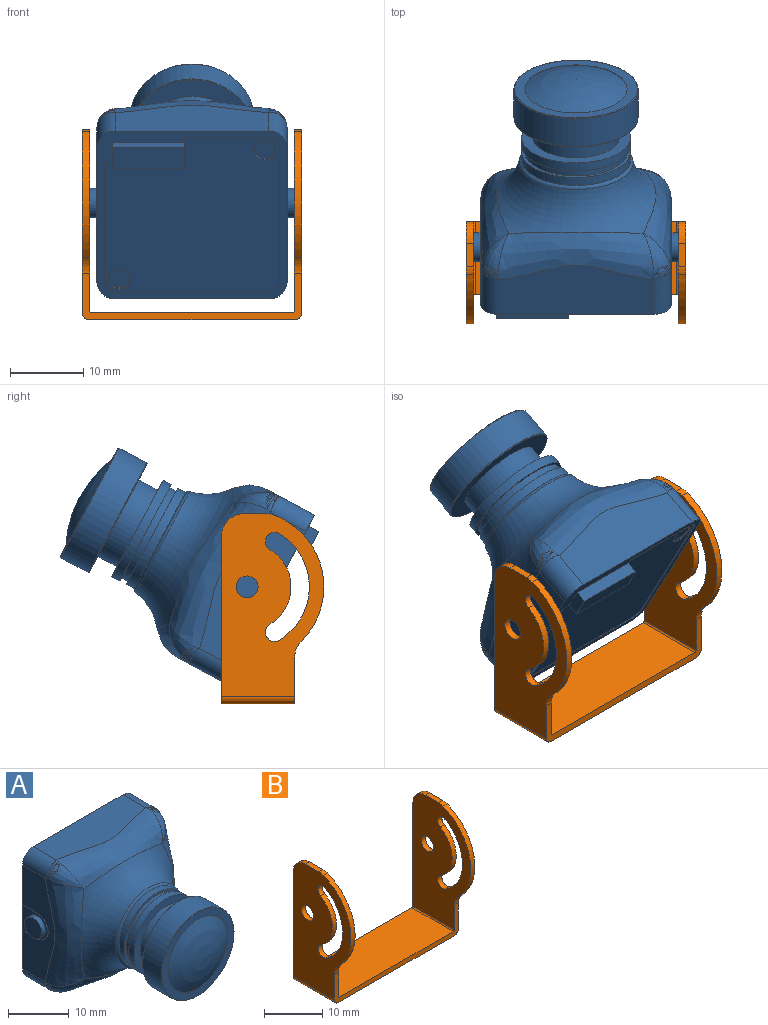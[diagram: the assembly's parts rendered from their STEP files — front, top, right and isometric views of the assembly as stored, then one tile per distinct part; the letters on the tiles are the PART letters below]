
ASSEMBLY  parts=2 mates=1
PART A: 86 faces, bbox 33.8x31.1x33.8 mm
  f0: torus R=12.35mm, axis (0,1,0), area 0mm2, adj f7,f31,f34
  f1: torus R=12.35mm, axis (0,1,0), area 0mm2, adj f8,f23,f26
  f2: torus R=12.35mm, axis (0,1,0), area 0mm2, adj f6,f28,f30
  f3: torus R=15.6mm, axis (0,1,0), area 402.5mm2, adj f5,f15,f16,f17,f18
  f4: torus R=12.35mm, axis (0,1,0), area 0mm2, adj f9,f19,f22
  f5: torus R=7.32mm, axis (0,1,0), area 33.3mm2, adj f3,f66
  f6: cylinder r=2.5mm len=5.66mm, axis (0,1,0), area 22mm2, adj f2,f10,f13,f14,f16,f18,f28,f30
  f7: cylinder r=2.5mm len=5.66mm, axis (0,1,0), area 22mm2, adj f0,f10,f11,f14,f17,f18,f31,f34
  f8: cylinder r=2.5mm len=5.66mm, axis (0,1,0), area 22mm2, adj f1,f11,f12,f14,f15,f17,f23,f26
  f9: cylinder r=2.5mm len=5.66mm, axis (0,1,0), area 22mm2, adj f4,f12,f13,f14,f15,f16,f19,f22
  f10: plane 21.01x7.56mm, normal (0,0,-1), area 137.3mm2, adj f6,f7,f14,f18
  f11: plane 21x7.56mm, normal (-1,0,0), area 109.5mm2, adj f7,f8,f14,f17,f58,f59,f60
  f12: plane 21x7.56mm, normal (0,0,1), area 137.3mm2, adj f8,f9,f14,f15
  f13: plane 21.01x7.56mm, normal (1,0,0), area 109.5mm2, adj f6,f9,f14,f16,f55,f56,f57
  f14: plane 26.25x26mm, normal (0,1,0), area 108.7mm2, adj f6,f7,f8,f9,f10,f11,f12,f13
  f15: bspline ~24.08x6.44mm, area 116mm2, adj f3,f8,f9,f12,f20,f22,f23,f24
  f16: bspline ~24.08x6.44mm, area 116mm2, adj f3,f6,f9,f13,f19,f20,f27,f28
  f17: bspline ~24.08x6.44mm, area 116mm2, adj f3,f7,f8,f11,f24,f26,f31,f32
  f18: bspline ~24.08x6.44mm, area 116mm2, adj f3,f6,f7,f10,f27,f30,f32,f34
  f19: bspline ~1.79x1.79mm, area 1.2mm2, adj f4,f9,f16,f21
  f20: bspline ~5.02x3.83mm, area 8.7mm2, adj f15,f16,f21
  f21: sphere r=2.4mm, area 2mm2, adj f19,f20,f22
  f22: bspline ~1.79x1.79mm, area 1.2mm2, adj f4,f9,f15,f21
  f23: bspline ~1.79x1.79mm, area 1.2mm2, adj f1,f8,f15,f25
  f24: bspline ~5.02x3.83mm, area 8.7mm2, adj f15,f17,f25
  f25: sphere r=2.4mm, area 2mm2, adj f23,f24,f26
  f26: bspline ~1.79x1.79mm, area 1.2mm2, adj f1,f8,f17,f25
  f27: bspline ~5.02x3.83mm, area 8.7mm2, adj f16,f18,f29
  f28: bspline ~1.79x1.79mm, area 1.2mm2, adj f2,f6,f16,f29
  f29: sphere r=2.4mm, area 2mm2, adj f27,f28,f30
  f30: bspline ~1.79x1.79mm, area 1.2mm2, adj f2,f6,f18,f29
  f31: bspline ~1.79x1.79mm, area 1.2mm2, adj f0,f7,f17,f33
  f32: bspline ~5.02x3.83mm, area 8.7mm2, adj f17,f18,f33
  f33: sphere r=2.4mm, area 2mm2, adj f31,f32,f34
  f34: bspline ~1.79x1.79mm, area 1.2mm2, adj f0,f7,f18,f33
  f35: plane 11.5x0.1mm, normal (0,0,1), area 1.1mm2, adj f14,f36,f43,f44
  f36: plane 4x1.7mm, normal (1,0,0), area 5.7mm2, adj f14,f35,f37,f44,f52,f53
  f37: plane 11x1.7mm, normal (0,0,1), area 16.9mm2, adj f14,f36,f38,f44,f51,f53
  f38: plane 18.5x0.1mm, normal (1,0,0), area 1.8mm2, adj f14,f37,f39,f44
  f39: cylinder r=1.5mm len=1.5mm, axis (0,1,0), area 0.2mm2, adj f14,f38,f40,f44
  f40: plane 21x0.1mm, normal (0,0,-1), area 2.1mm2, adj f14,f39,f41,f44
  f41: cylinder r=1.5mm len=1.5mm, axis (0,1,0), area 0.2mm2, adj f14,f40,f42,f44
  f42: plane 21x0.1mm, normal (-1,0,0), area 2.1mm2, adj f14,f41,f43,f44
  f43: cylinder r=1.5mm len=1.5mm, axis (0,1,0), area 0.2mm2, adj f14,f35,f42,f44
  f44: plane 24x24mm, normal (0,1,0), area 516.4mm2, adj f35,f36,f37,f38,f39,f40,f41,f42
  f45: cylinder r=1.4mm len=2.8mm, axis (0,1,0), area 0.9mm2, adj f46,f49
  f46: plane 2.8x2.8mm, normal (0,1,0), area 6.2mm2, adj f45
  f47: cylinder r=1.4mm len=2.8mm, axis (0,1,0), area 0.9mm2, adj f48,f50
  f48: plane 2.8x2.8mm, normal (0,1,0), area 6.2mm2, adj f47
  f49: cone r=1.4mm half-angle=45deg, axis (0,1,0), area 1.3mm2, adj f44,f45
  f50: cone r=1.4mm half-angle=45deg, axis (0,1,0), area 1.3mm2, adj f44,f47
  f51: plane 3.3x1.6mm, normal (-1,0,0), area 5.3mm2, adj f14,f37,f52,f53
  f52: plane 9.9x1.6mm, normal (0,0,-1), area 15.8mm2, adj f14,f36,f51,f53
  f53: plane 9.9x3.3mm, normal (0,1,0), area 32.7mm2, adj f36,f37,f51,f52
  f54: plane 6x5.3mm, normal (1,0,0), area 15.3mm2, adj f14,f55,f56,f57,f64
  f55: cylinder r=2.5mm len=5mm, axis (-1,0,0), area 1mm2, adj f13,f54,f56,f57
  f56: plane 3.61x0.15mm, normal (0,-0.04,1), area 0.5mm2, adj f13,f14,f54,f55
  f57: plane 3.61x0.15mm, normal (0,-0.04,-1), area 0.5mm2, adj f13,f14,f54,f55
  f58: plane 3.61x0.15mm, normal (0,-0.04,-1), area 0.5mm2, adj f11,f14,f60,f61
  f59: plane 3.61x0.15mm, normal (0,-0.04,1), area 0.5mm2, adj f11,f14,f60,f61
  f60: cylinder r=2.5mm len=5mm, axis (-1,0,0), area 1mm2, adj f11,f58,f59,f61
  f61: plane 6x5.3mm, normal (-1,0,0), area 15.3mm2, adj f14,f58,f59,f60,f63
  f62: plane 4x4mm, normal (-1,0,0), area 12.6mm2, adj f63
  f63: cylinder r=2mm len=4mm, axis (-1,0,0), area 11mm2, adj f61,f62
  f64: cylinder r=2mm len=4mm, axis (-1,0,0), area 11mm2, adj f54,f65
  f65: plane 4x4mm, normal (1,0,0), area 12.6mm2, adj f64
  f66: plane 14.9x14.9mm, normal (0,1,0), area 6mm2, adj f5,f67
  f67: cylinder r=7.45mm len=14.9mm, axis (0,1,0), area 58.5mm2, adj f66,f69
  f68: plane 14.9x14.9mm, normal (0,1,0), area 20.4mm2, adj f70,f78
  f69: plane 14.9x14.9mm, normal (0,-1,0), area 20.4mm2, adj f67,f70
  f70: cylinder r=7mm len=14mm, axis (0,-1,0), area 44mm2, adj f68,f69
  f71: sphere r=16mm, area 162.1mm2, adj f72
  f72: cylinder r=7mm len=14mm, axis (0,-1,0), area 4.4mm2, adj f71,f73
  f73: plane 16.8x16.8mm, normal (0,-1,0), area 67.7mm2, adj f72,f80
  f74: cylinder r=8.5mm len=17mm, axis (0,1,0), area 229.7mm2, adj f79,f80
  f75: plane 16.8x16.8mm, normal (0,1,0), area 111.4mm2, adj f76,f79
  f76: cylinder r=5.92mm len=11.85mm, axis (0,1,0), area 111.7mm2, adj f75,f77
  f77: plane 14.9x14.9mm, normal (0,-1,0), area 64.1mm2, adj f76,f78
  f78: cylinder r=7.45mm len=14.9mm, axis (0,1,0), area 58.5mm2, adj f68,f77
  f79: torus R=8.4mm, axis (0,-1,0), area 8.4mm2, adj f74,f75
  f80: torus R=8.4mm, axis (0,-1,0), area 8.4mm2, adj f73,f74
  f81: plane 11.15x3.93mm, normal (0,-1,0), area 31.9mm2, adj f83,f84
  f82: plane 11.15x3.93mm, normal (0,-1,0), area 31.9mm2, adj f83,f84
  f83: cylinder r=2.5mm len=11.15mm, axis (-1,0,0), area 51.7mm2, adj f81,f82,f84
  f84: cylinder r=5.92mm len=12mm, axis (0,-1,0), area 446.7mm2, adj f81,f82,f83,f85
  f85: plane 11.85x11.85mm, normal (0,1,0), area 110.3mm2, adj f84
PART B: 32 faces, bbox 30x14x26 mm
  f0: plane 3.19x1mm, normal (0,0,1), area 3.2mm2, adj f13,f22,f24,f29
  f1: cylinder r=3mm len=1.08mm, axis (-1,0,0), area 1.1mm2, adj f2,f12,f23,f28
  f2: cylinder r=10.5mm len=17.26mm, axis (-1,0,0), area 20.9mm2, adj f1,f3,f23,f28
  f3: cylinder r=3mm len=2.13mm, axis (-1,0,0), area 2.4mm2, adj f2,f4,f23,f28
  f4: plane 30x6.41mm, normal (0,-1,0), area 40.4mm2, adj f3,f15,f16,f23,f24,f25,f26,f27
  f5: plane 30x23mm, normal (0,1,0), area 73.6mm2, adj f11,f16,f22,f23,f24,f25,f26,f27
  f6: cylinder r=8.5mm len=14.55mm, axis (-1,0,0), area 17.5mm2, adj f7,f9,f23,f28
  f7: cylinder r=1.25mm len=2.32mm, axis (-1,0,0), area 3.9mm2, adj f6,f8,f23,f28
  f8: cylinder r=6mm len=10.27mm, axis (-1,0,0), area 12.3mm2, adj f7,f9,f23,f28
  f9: cylinder r=1.25mm len=2.32mm, axis (-1,0,0), area 3.9mm2, adj f6,f8,f23,f28
  f10: cylinder r=1.5mm len=3mm, axis (-1,0,0), area 9.4mm2, adj f23,f28
  f11: cylinder r=3mm len=3mm, axis (-1,0,0), area 4.7mm2, adj f5,f12,f23,f28
  f12: plane 3.19x1mm, normal (0,0,1), area 3.2mm2, adj f1,f11,f23,f28
  f13: cylinder r=3mm len=1.08mm, axis (-1,0,0), area 1.1mm2, adj f0,f14,f24,f29
  f14: cylinder r=10.5mm len=17.26mm, axis (-1,0,0), area 20.9mm2, adj f13,f15,f24,f29
  f15: cylinder r=3mm len=2.13mm, axis (-1,0,0), area 2.4mm2, adj f4,f14,f24,f29
  f16: plane 28x10mm, normal (0,0,-1), area 280mm2, adj f4,f5,f25,f26
  f17: cylinder r=8.5mm len=14.55mm, axis (-1,0,0), area 17.5mm2, adj f18,f20,f24,f29
  f18: cylinder r=1.25mm len=2.32mm, axis (-1,0,0), area 3.9mm2, adj f17,f19,f24,f29
  f19: cylinder r=6mm len=10.27mm, axis (-1,0,0), area 12.3mm2, adj f18,f20,f24,f29
  f20: cylinder r=1.25mm len=2.32mm, axis (-1,0,0), area 3.9mm2, adj f17,f19,f24,f29
  f21: cylinder r=1.5mm len=3mm, axis (-1,0,0), area 9.4mm2, adj f24,f29
  f22: cylinder r=3mm len=3mm, axis (-1,0,0), area 4.7mm2, adj f0,f5,f24,f29
  f23: plane 25x14mm, normal (1,0,0), area 242.6mm2, adj f1,f2,f3,f4,f5,f6,f7,f8
  f24: plane 25x14mm, normal (-1,0,0), area 242.6mm2, adj f0,f4,f5,f13,f14,f15,f17,f18
  f25: cylinder r=1mm len=10mm, axis (0,1,0), area 15.7mm2, adj f4,f5,f16,f24
  f26: cylinder r=1mm len=10mm, axis (0,-1,0), area 15.7mm2, adj f4,f5,f16,f23
  f27: plane 27.5x10mm, normal (0,0,1), area 275mm2, adj f4,f5,f30,f31
  f28: plane 24.75x14mm, normal (-1,0,0), area 240.1mm2, adj f1,f2,f3,f4,f5,f6,f7,f8
  f29: plane 24.75x14mm, normal (1,0,0), area 240.1mm2, adj f0,f4,f5,f13,f14,f15,f17,f18
  f30: cylinder r=0.25mm len=10mm, axis (0,1,0), area 3.9mm2, adj f4,f5,f27,f28
  f31: cylinder r=0.25mm len=10mm, axis (0,-1,0), area 3.9mm2, adj f4,f5,f27,f29
PLACE A rot(axis=(-1,0,0),151.9deg) t=(0,-1.59,1.35)mm
PLACE B at identity fixed
MATE revolute A.f55 <-> B.f2  axis (-1,0,0) through (-14,1.5,3)mm
